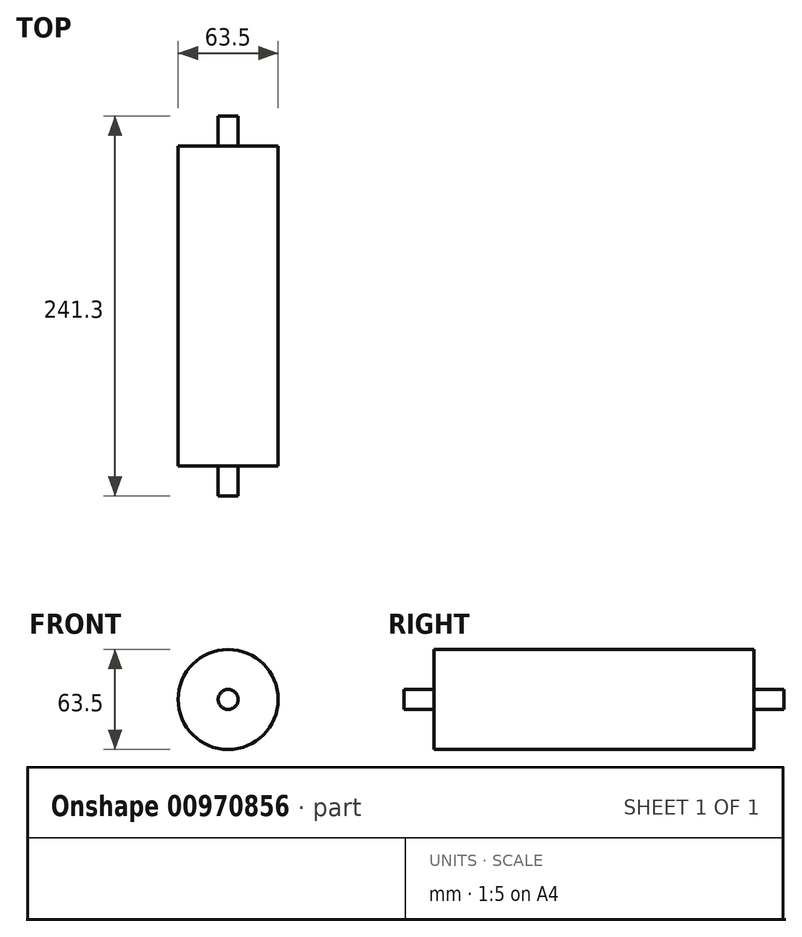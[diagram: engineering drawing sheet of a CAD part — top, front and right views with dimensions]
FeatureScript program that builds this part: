
annotation { "Feature Type Name" : "Feature", "Feature Type Description" : "" }
export const myFeature = defineFeature(function(context is Context, id is Id, definition is map)
    precondition{}
    {
        {
            var Q0;
            Q0=qCreatedBy(makeId("Front.planeOp"),FACE);
            var sketch = newSketch(context, id + "F0", { "sketchPlane" : qUnion([Q0])});
            skCircle(sketch, "E0", {"center": v(0, 0) * mm, "radius": 31.75 * mm});
            skSolve(sketch);
        }
        {
            var Q0;
            Q0=makeQuery(id+"F0.imprint","IMPRINT",FACE,{"disambiguationData":[TD([[makeQuery(id+"F0.imprint","IMPRINT",EDGE,{"derivedFrom":sQuery(id+"F0.wireOp",EDGE,"E0")}),1.0]])]});
            extrude(context, id + "F1", {"entities" : qUnion([Q0]), "depth" : 203.2 * mm, "offsetDistance" : 25.4 * mm});
        }
        {
            var Q0;
            Q0=makeQuery(id+"F1.opExtrude","CAP_FACE",FACE,{"disambiguationData":[OSD([sQuery(id+"F0.wireOp",EDGE,"E0")])],"isStart":false});
            var sketch = newSketch(context, id + "F2", { "sketchPlane" : qUnion([Q0])});
            skCircle(sketch, "E1", {"center": v(0, 0) * mm, "radius": 6.35 * mm});
            skSolve(sketch);
        }
        {
            var Q0;
            Q0=makeQuery(id+"F2.imprint","IMPRINT",FACE,{"disambiguationData":[TD([[makeQuery(id+"F2.imprint","IMPRINT",EDGE,{"derivedFrom":sQuery(id+"F2.wireOp",EDGE,"E1")}),1.0]])]});
            extrude(context, id + "F3", {"entities" : qUnion([Q0]), "operationType" : NewBodyOperationType.ADD, "depth" : 19.05 * mm, "offsetDistance" : 25.4 * mm});
        }
        {
            var Q0;
            Q0=makeQuery(id+"F1.opExtrude","CAP_FACE",FACE,{"disambiguationData":[OSD([sQuery(id+"F0.wireOp",EDGE,"E0")])],"isStart":true});
            var sketch = newSketch(context, id + "F4", { "sketchPlane" : qUnion([Q0])});
            skCircle(sketch, "E2", {"center": v(0, 0) * mm, "radius": 6.35 * mm});
            skSolve(sketch);
        }
        {
            var Q0;
            Q0=makeQuery(id+"F4.imprint","IMPRINT",FACE,{"disambiguationData":[TD([[makeQuery(id+"F4.imprint","IMPRINT",EDGE,{"derivedFrom":sQuery(id+"F4.wireOp",EDGE,"E2")}),1.0]])]});
            extrude(context, id + "F5", {"entities" : qUnion([Q0]), "operationType" : NewBodyOperationType.ADD, "depth" : 19.05 * mm, "offsetDistance" : 25.4 * mm});
        }
    });
